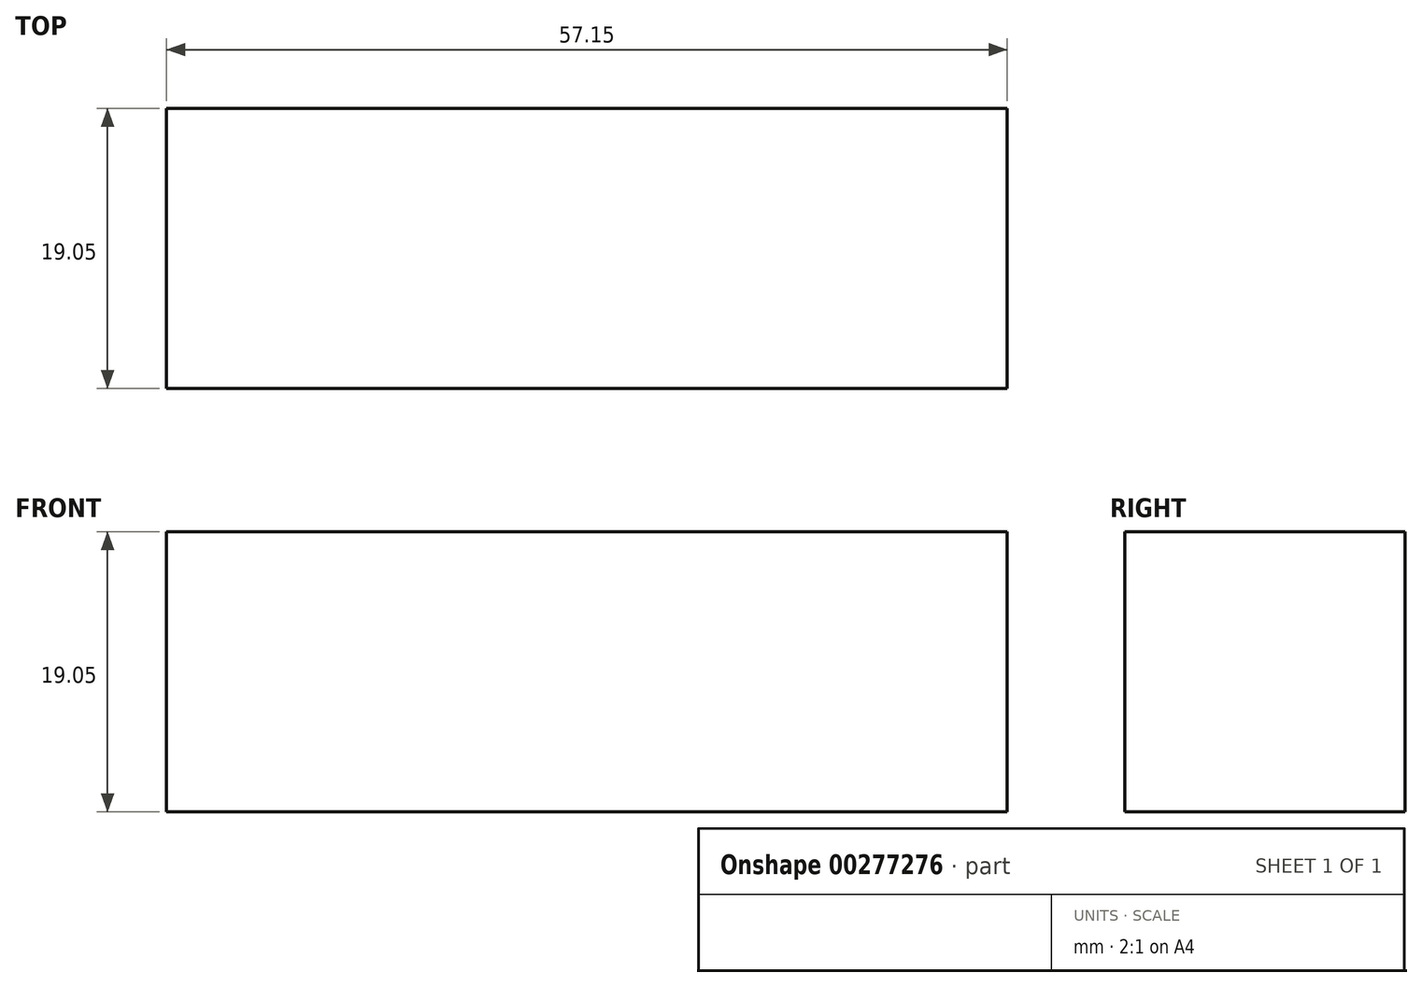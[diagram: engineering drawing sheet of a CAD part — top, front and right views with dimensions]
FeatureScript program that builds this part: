
annotation { "Feature Type Name" : "Feature", "Feature Type Description" : "" }
export const myFeature = defineFeature(function(context is Context, id is Id, definition is map)
    precondition{}
    {
        {
            var Q0;
            Q0=qCreatedBy(makeId("Top.planeOp"),FACE);
            var sketch = newSketch(context, id + "F0", { "sketchPlane" : qUnion([Q0])});
            skLineSegment(sketch, "E0.bottom", {"start": v(-37.15, -46.45) * mm, "end": v(-18.1, -46.45) * mm});
            skLineSegment(sketch, "E0.top", {"start": v(-37.15, -65.5) * mm, "end": v(-18.1, -65.5) * mm});
            skLineSegment(sketch, "E0.left", {"start": v(-37.15, -46.45) * mm, "end": v(-37.15, -65.5) * mm});
            skLineSegment(sketch, "E0.right", {"start": v(-18.1, -46.45) * mm, "end": v(-18.1, -65.5) * mm});
            skLineSegment(sketch, "E1.bottom", {"start": v(-18.1, -46.45) * mm, "end": v(0.95, -46.45) * mm});
            skLineSegment(sketch, "E1.top", {"start": v(-18.1, -65.5) * mm, "end": v(0.95, -65.5) * mm});
            skLineSegment(sketch, "E1.right", {"start": v(0.95, -46.45) * mm, "end": v(0.95, -65.5) * mm});
            skLineSegment(sketch, "E2.bottom", {"start": v(0.95, -46.45) * mm, "end": v(20, -46.45) * mm});
            skLineSegment(sketch, "E2.top", {"start": v(0.95, -65.5) * mm, "end": v(20, -65.5) * mm});
            skLineSegment(sketch, "E2.right", {"start": v(20, -46.45) * mm, "end": v(20, -65.5) * mm});
            skLineSegment(sketch, "E3.bottom", {"start": v(20, -46.45) * mm, "end": v(0.95, -46.45) * mm});
            skLineSegment(sketch, "E3.top", {"start": v(20, -27.4) * mm, "end": v(0.95, -27.4) * mm});
            skLineSegment(sketch, "E3.left", {"start": v(20, -46.45) * mm, "end": v(20, -27.4) * mm});
            skLineSegment(sketch, "E3.right", {"start": v(0.95, -46.45) * mm, "end": v(0.95, -27.4) * mm});
            skLineSegment(sketch, "E4.bottom", {"start": v(0.95, -27.4) * mm, "end": v(20, -27.4) * mm});
            skLineSegment(sketch, "E4.top", {"start": v(0.95, -8.35) * mm, "end": v(20, -8.35) * mm});
            skLineSegment(sketch, "E4.left", {"start": v(0.95, -27.4) * mm, "end": v(0.95, -8.35) * mm});
            skLineSegment(sketch, "E4.right", {"start": v(20, -27.4) * mm, "end": v(20, -8.35) * mm});
            skSolve(sketch);
        }
        {
            var Q0;
            Q0=makeQuery(id+"F0.imprint","IMPRINT",FACE,{"disambiguationData":[TD([[makeQuery(id+"F0.imprint","IMPRINT",EDGE,{"derivedFrom":sQuery(id+"F0.wireOp",EDGE,"E4.bottom")}),1.0]])]});
            var Q1;
            Q1=makeQuery(id+"F0.imprint","IMPRINT",FACE,{"disambiguationData":[TD([[makeQuery(id+"F0.imprint","IMPRINT",EDGE,{"derivedFrom":sQuery(id+"F0.wireOp",EDGE,"E3.bottom")}),-1.0]])]});
            var Q2;
            Q2=makeQuery(id+"F0.imprint","IMPRINT",FACE,{"disambiguationData":[TD([[makeQuery(id+"F0.imprint","IMPRINT",EDGE,{"derivedFrom":sQuery(id+"F0.wireOp",EDGE,"E2.top")}),1.0]])]});
            var Q3;
            Q3=makeQuery(id+"F0.imprint","IMPRINT",FACE,{"disambiguationData":[TD([[makeQuery(id+"F0.imprint","IMPRINT",EDGE,{"derivedFrom":sQuery(id+"F0.wireOp",EDGE,"E0.bottom")}),-1.0]])]});
            var Q4;
            Q4=makeQuery(id+"F0.imprint","IMPRINT",FACE,{"disambiguationData":[TD([[makeQuery(id+"F0.imprint","IMPRINT",EDGE,{"derivedFrom":sQuery(id+"F0.wireOp",EDGE,"E1.bottom")}),-1.0]])]});
            extrude(context, id + "F1", {"entities" : qUnion([Q0, Q1, Q2, Q3, Q4]), "depth" : 19.05 * mm});
        }
    });
